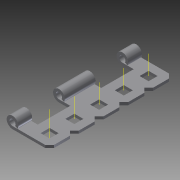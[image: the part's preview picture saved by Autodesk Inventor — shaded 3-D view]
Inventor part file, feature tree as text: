
AUTODESK INVENTOR PART (.ipt)
format: ipt  version: 2015 (Build 190159000, 159)  size: 161,280 bytes
history: native  units: in
note: dims shown in document units (in); Inventor stores cm internally (conversion verified against a paired STEP export)
features: other x8, pattern_linear x1, imported_body x1
ambient origin geometry x8: Origin, YZ Plane, XZ Plane, XY Plane, X Axis, Y Axis, Z Axis, Center Point
bodies: Body1 (feature_tree)
feature tree (10):
  other  "Cut-Extrude3"
  other  "Hinge Plate"
  other  "axis"
  pattern_linear  "Rectangular Pattern1"  Count1=5 Spacing1=0.5in
  imported_body  "Base1"
  other  "Work Point1"
  other  "Work Axis2"
  other  "Work Axis3"
  other  "Work Axis4"
  other  "Work Axis5"
